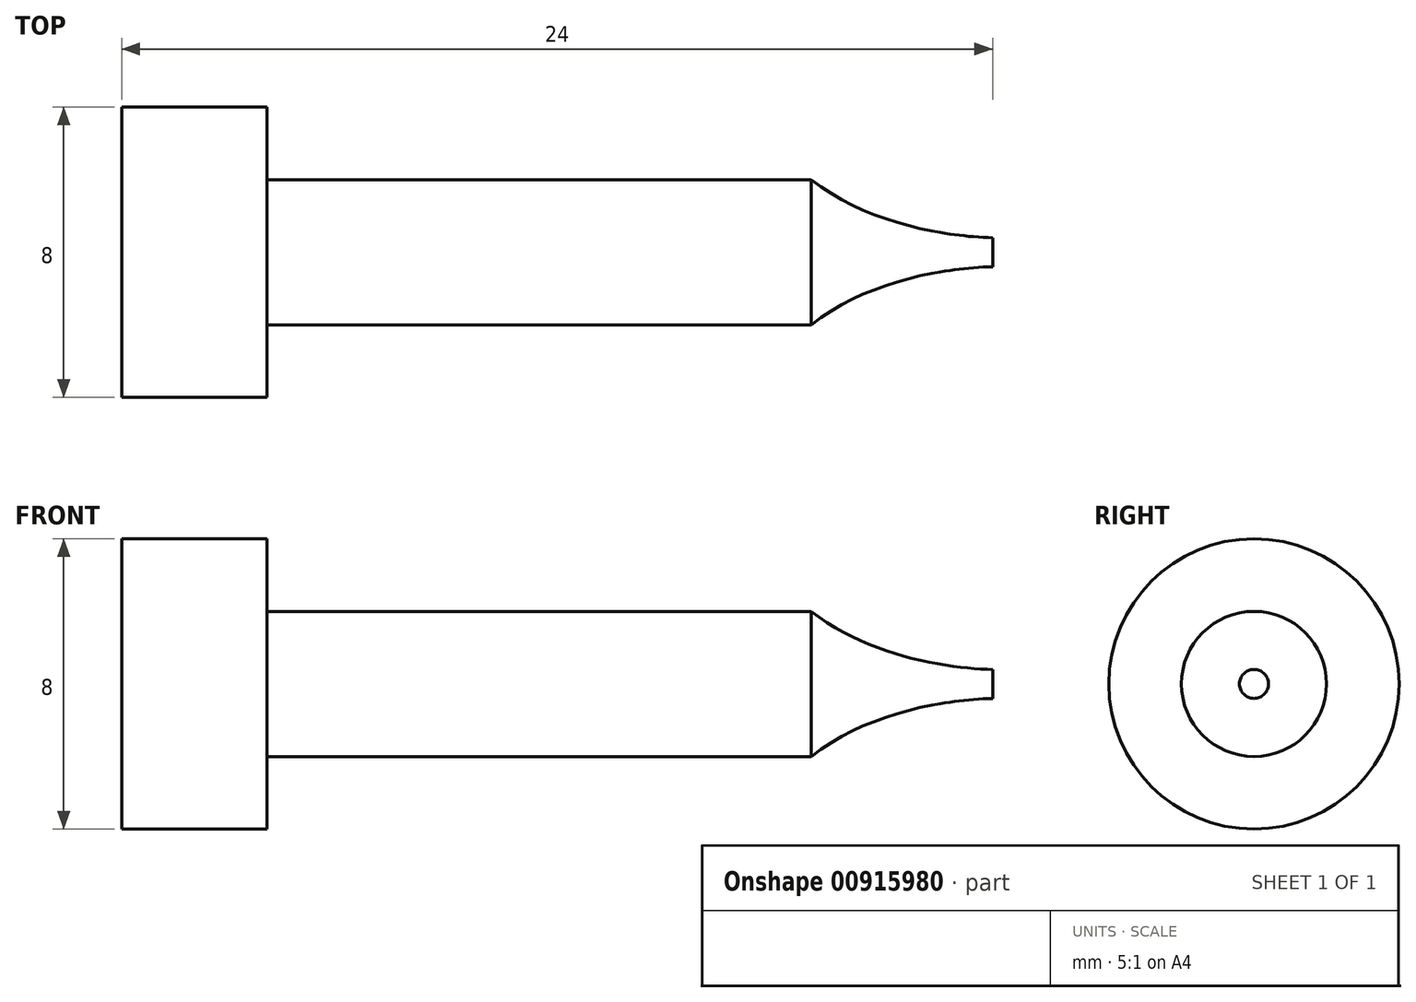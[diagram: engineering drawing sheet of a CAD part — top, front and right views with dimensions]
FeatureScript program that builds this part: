
annotation { "Feature Type Name" : "Feature", "Feature Type Description" : "" }
export const myFeature = defineFeature(function(context is Context, id is Id, definition is map)
    precondition{}
    {
        {
            var Q0;
            Q0=qCreatedBy(makeId("Front.planeOp"),FACE);
            var sketch = newSketch(context, id + "F0", { "sketchPlane" : qUnion([Q0])});
            skLineSegment(sketch, "E0", {"start": v(-15, 2) * mm, "end": v(0, 2) * mm});
            skLineSegment(sketch, "E1", {"start": v(5, 0) * mm, "end": v(5, 0.4) * mm});
            skFitSpline(sketch, "E2", {"points": [v(0, 2) * mm, v(5, 0.4) * mm], "startDerivative": vector(4.8, -3.79) * mm, "endDerivative": vector(3.46, -0.07) * mm});
            skLineSegment(sketch, "E3", {"start": v(-15, 2) * mm, "end": v(-15, 4) * mm});
            skLineSegment(sketch, "E4", {"start": v(-15, 4) * mm, "end": v(-19, 4) * mm});
            skLineSegment(sketch, "E5", {"start": v(-19, 4) * mm, "end": v(-19, 0) * mm});
            skLineSegment(sketch, "E6", {"start": v(-19, 0) * mm, "end": v(5, 0) * mm});
            skSolve(sketch);
        }
        {
            var Q0;
            Q0 = qSketchRegion(id + "F0", true);
            var Q1;
            Q1=sQuery(id+"F0.wireOp",EDGE,"E6");
            revolve(context, id + "F1", {"surfaceOperationType" : NewSurfaceOperationType.NEW, "entities" : qUnion([Q0]), "axis" : qUnion([Q1]), "revolveType" : RevolveType.FULL});
        }
    });
